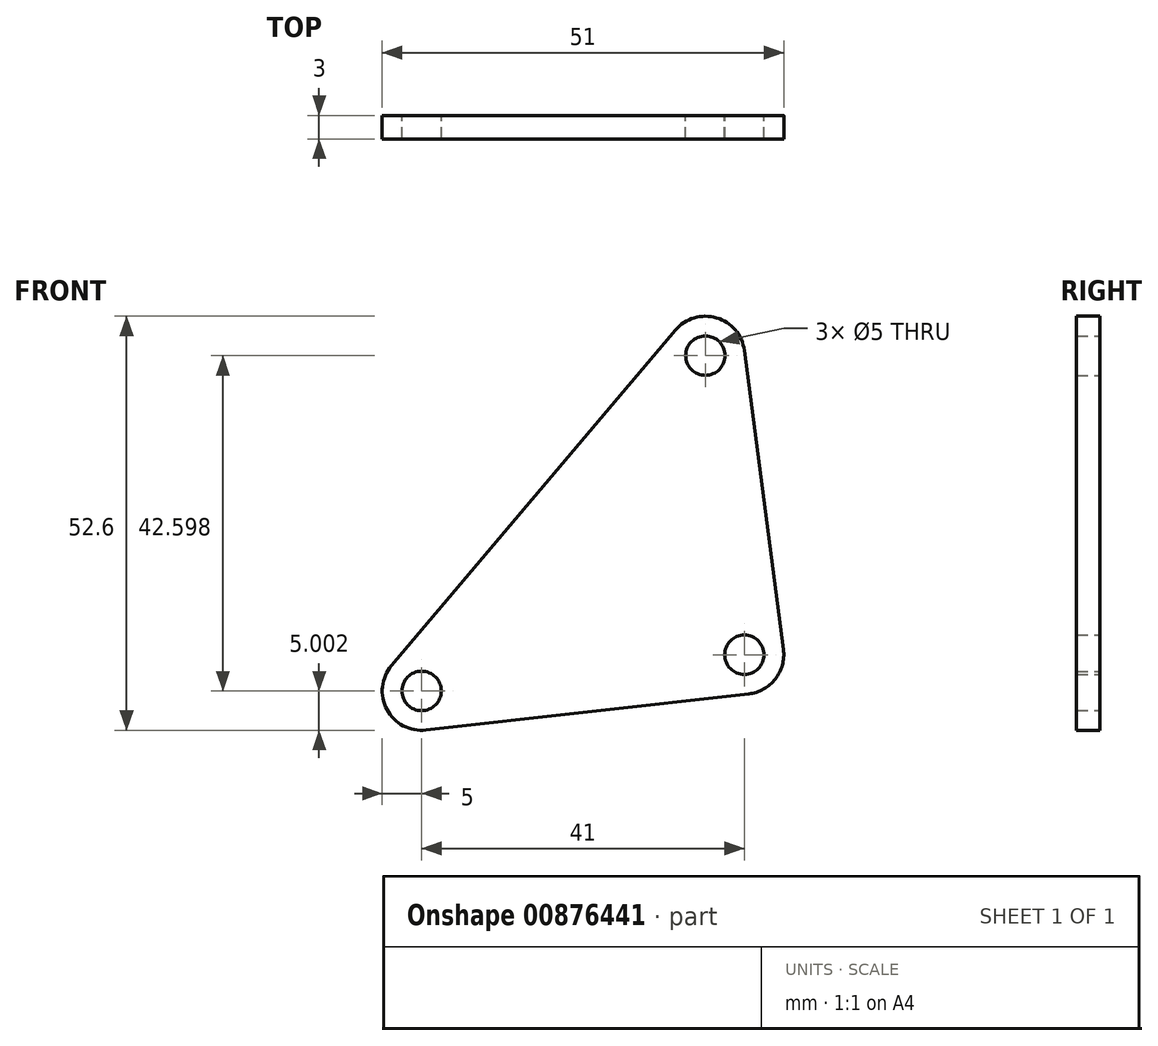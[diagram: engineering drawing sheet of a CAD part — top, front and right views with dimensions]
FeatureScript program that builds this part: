
annotation { "Feature Type Name" : "Feature", "Feature Type Description" : "" }
export const myFeature = defineFeature(function(context is Context, id is Id, definition is map)
    precondition{}
    {
        {
            var Q0;
            Q0=qCreatedBy(makeId("Front.planeOp"),FACE);
            var sketch = newSketch(context, id + "F0", { "sketchPlane" : qUnion([Q0])});
            skLineSegment(sketch, "E0", {"start": v(4.96, 0.65) * mm, "end": v(0, 38.65) * mm});
            skLineSegment(sketch, "E1", {"start": v(-8.78, 41.23) * mm, "end": v(-44.82, -1.37) * mm});
            skLineSegment(sketch, "E2", {"start": v(-40.44, -9.57) * mm, "end": v(0.56, -4.97) * mm});
            skArc(sketch, "E3.filletArc", {"start": v(-44.82, -1.37) * mm, "mid": v(-45.41, -6.95) * mm, "end": v(-40.44, -9.57) * mm});
            skPoint(sketch, "E4.visualSharp", {"position": v(0, 0) * mm});
            skArc(sketch, "E4.filletArc", {"start": v(0.56, -4.97) * mm, "mid": v(3.94, -3.08) * mm, "end": v(4.96, 0.65) * mm});
            skArc(sketch, "E5.filletArc", {"start": v(0, 38.65) * mm, "mid": v(-3.55, 42.8) * mm, "end": v(-8.78, 41.23) * mm});
            skCircle(sketch, "E6", {"center": v(-41, -4.6) * mm, "radius": 2.5 * mm});
            skCircle(sketch, "E7", {"center": v(-4.96, 38) * mm, "radius": 2.5 * mm});
            skCircle(sketch, "E8", {"center": v(0, 0) * mm, "radius": 2.5 * mm});
            skSolve(sketch);
        }
        {
            var Q0;
            Q0=makeQuery(id+"F0.imprint","IMPRINT",FACE,{"disambiguationData":[TD([[makeQuery(id+"F0.imprint","IMPRINT",EDGE,{"derivedFrom":sQuery(id+"F0.wireOp",EDGE,"E0")}),1.0]])]});
            extrude(context, id + "F1", {"entities" : qUnion([Q0]), "depth" : 3 * mm, "offsetDistance" : 25 * mm});
        }
    });
